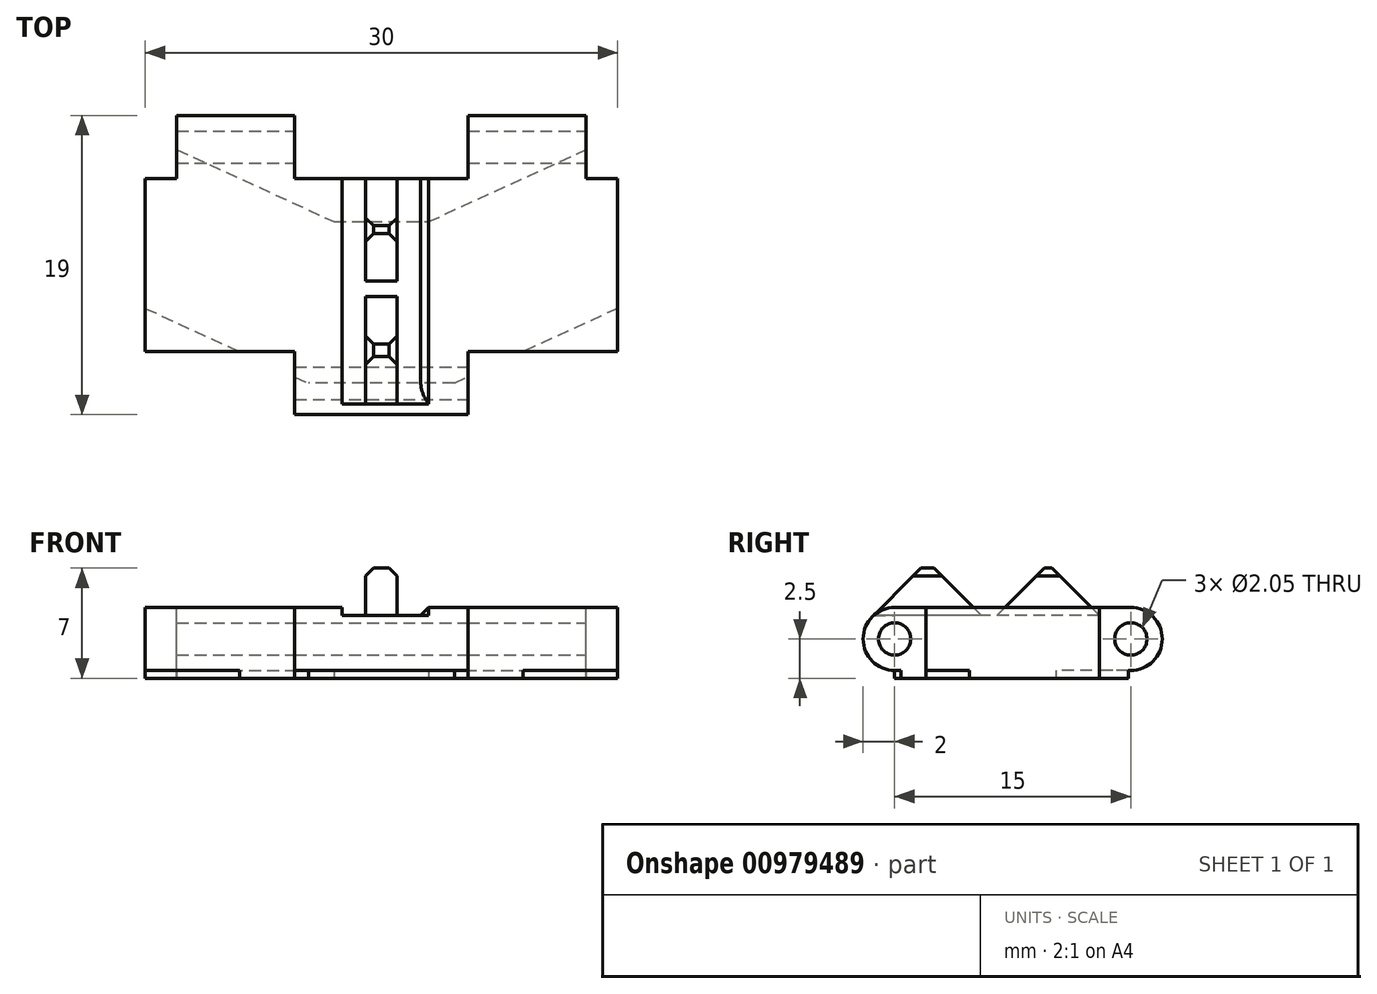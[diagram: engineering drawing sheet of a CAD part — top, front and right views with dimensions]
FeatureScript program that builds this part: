
annotation { "Feature Type Name" : "Feature", "Feature Type Description" : "" }
export const myFeature = defineFeature(function(context is Context, id is Id, definition is map)
    precondition{}
    {
        {
            var Q0;
            Q0=qCreatedBy(makeId("Top.planeOp"),FACE);
            var sketch = newSketch(context, id + "F0", { "sketchPlane" : qUnion([Q0])});
            skLineSegment(sketch, "E0.bottom", {"start": v(15, -7.5) * mm, "end": v(-15, -7.5) * mm});
            skLineSegment(sketch, "E0.top", {"start": v(15, 7.5) * mm, "end": v(-15, 7.5) * mm});
            skLineSegment(sketch, "E0.left", {"start": v(15, -7.5) * mm, "end": v(15, 7.5) * mm});
            skLineSegment(sketch, "E0.right", {"start": v(-15, -7.5) * mm, "end": v(-15, 7.5) * mm});
            skPoint(sketch, "E0.middle", {"position": v(0, 0) * mm});
            skSolve(sketch);
        }
        {
            var Q0;
            Q0=makeQuery(id+"F0.imprint","IMPRINT",FACE,{"disambiguationData":[TD([[makeQuery(id+"F0.imprint","IMPRINT",EDGE,{"derivedFrom":sQuery(id+"F0.wireOp",EDGE,"E0.bottom")}),-1.0]])]});
            extrude(context, id + "F1", {"entities" : qUnion([Q0]), "depth" : 4.5 * mm, "offsetDistance" : 25 * mm});
        }
        {
            var Q0;
            Q0=makeQuery(id+"F1.opExtrude","SWEPT_FACE",FACE,{"disambiguationData":[OSD([sQuery(id+"F0.wireOp",EDGE,"E0.right")])]});
            var sketch = newSketch(context, id + "F2", { "sketchPlane" : qUnion([Q0])});
            skCircle(sketch, "E1", {"center": v(-7.5, 2.5) * mm, "radius": 2 * mm});
            skCircle(sketch, "E2", {"center": v(7.5, 2.5) * mm, "radius": 2 * mm});
            skSolve(sketch);
        }
        {
            var Q0;
            {var subQ0=sQuery(id+"F2.wireOp",EDGE,"vetQoRZT-xKbi-iN1l-QBYZ-xdwohGv9bb5s");var subQ1=sQuery(id+"F0.wireOp",EDGE,"E0.right");var subQ2=makeQuery(id+"F1.opExtrude","SWEPT_EDGE",EDGE,{"disambiguationData":[OSD([sQuery(id+"F0.wireOp",EDGE,"E0.top"),subQ1])]});var subQ3=makeQuery(id+"F2.imprint","INTERSECT",VERTEX,{"disambiguationData":[OD(0.0)],"derivedFrom":[subQ2,subQ0]});Q0=makeQuery(id+"F2.imprint","IMPRINT",FACE,{"disambiguationData":[TD([[makeQuery(id+"F2.imprint","IMPRINT",EDGE,{"disambiguationData":[TD([[subQ3,-1.0]])],"derivedFrom":subQ0}),-1.0]])]});}
            var Q1;
            {var subQ0=sQuery(id+"F2.wireOp",EDGE,"k2q76aXO-4BDj-htHJ-C2at-5MqpkDl38XXc");var subQ1=sQuery(id+"F0.wireOp",EDGE,"E0.right");var subQ2=makeQuery(id+"F1.opExtrude","SWEPT_EDGE",EDGE,{"disambiguationData":[OSD([sQuery(id+"F0.wireOp",EDGE,"E0.bottom"),subQ1])]});var subQ3=makeQuery(id+"F2.imprint","INTERSECT",VERTEX,{"disambiguationData":[OD(0.0)],"derivedFrom":[subQ2,subQ0]});Q1=makeQuery(id+"F2.imprint","IMPRINT",FACE,{"disambiguationData":[TD([[makeQuery(id+"F2.imprint","IMPRINT",EDGE,{"disambiguationData":[TD([[subQ3,1.0]])],"derivedFrom":subQ0}),-1.0]])]});}
            var Q2;
            {var subQ0=sQuery(id+"F2.wireOp",EDGE,"E1");var subQ1=sQuery(id+"F0.wireOp",EDGE,"E0.right");var subQ2=makeQuery(id+"F1.opExtrude","SWEPT_EDGE",EDGE,{"disambiguationData":[OSD([sQuery(id+"F0.wireOp",EDGE,"E0.top"),subQ1])]});var subQ4=makeQuery(id+"F2.imprint","INTERSECT",VERTEX,{"derivedFrom":[subQ2,subQ0]});Q2=makeQuery(id+"F2.imprint","IMPRINT",FACE,{"disambiguationData":[TD([[makeQuery(id+"F2.imprint","IMPRINT",EDGE,{"disambiguationData":[TD([[subQ4,1.0]])],"derivedFrom":subQ0}),1.0]])]});}
            var Q3;
            {var subQ0=sQuery(id+"F2.wireOp",EDGE,"E1");var subQ1=sQuery(id+"F0.wireOp",EDGE,"E0.right");var subQ2=makeQuery(id+"F1.opExtrude","SWEPT_EDGE",EDGE,{"disambiguationData":[OSD([sQuery(id+"F0.wireOp",EDGE,"E0.top"),subQ1])]});var subQ4=makeQuery(id+"F2.imprint","INTERSECT",VERTEX,{"derivedFrom":[subQ2,subQ0]});Q3=makeQuery(id+"F2.imprint","IMPRINT",FACE,{"disambiguationData":[TD([[makeQuery(id+"F2.imprint","IMPRINT",EDGE,{"disambiguationData":[TD([[subQ4,-1.0]])],"derivedFrom":subQ0}),1.0]])]});}
            var Q4;
            {var subQ0=sQuery(id+"F2.wireOp",EDGE,"E2");var subQ1=sQuery(id+"F0.wireOp",EDGE,"E0.right");var subQ2=makeQuery(id+"F1.opExtrude","SWEPT_EDGE",EDGE,{"disambiguationData":[OSD([sQuery(id+"F0.wireOp",EDGE,"E0.bottom"),subQ1])]});var subQ4=makeQuery(id+"F2.imprint","INTERSECT",VERTEX,{"derivedFrom":[subQ2,subQ0]});Q4=makeQuery(id+"F2.imprint","IMPRINT",FACE,{"disambiguationData":[TD([[makeQuery(id+"F2.imprint","IMPRINT",EDGE,{"disambiguationData":[TD([[subQ4,-1.0]])],"derivedFrom":subQ0}),1.0]])]});}
            extrude(context, id + "F3", {"entities" : qUnion([Q0, Q1, Q2, Q3, Q4]), "operationType" : NewBodyOperationType.ADD, "oppositeDirection" : true, "depth" : 30 * mm, "offsetDistance" : 25 * mm});
        }
        {
            var Q0;
            Q0=makeQuery(id+"F1.opExtrude","CAP_FACE",FACE,{"disambiguationData":[OSD([sQuery(id+"F0.wireOp",EDGE,"E0.bottom"),sQuery(id+"F0.wireOp",EDGE,"E0.top"),sQuery(id+"F0.wireOp",EDGE,"E0.left"),sQuery(id+"F0.wireOp",EDGE,"E0.right")])],"isStart":false});
            var sketch = newSketch(context, id + "F4", { "sketchPlane" : qUnion([Q0])});
            skLineSegment(sketch, "E3.bottom", {"start": v(-13, 7.5) * mm, "end": v(-5.5, 7.5) * mm});
            skLineSegment(sketch, "E3.top", {"start": v(-13, 9.5) * mm, "end": v(-5.5, 9.5) * mm});
            skLineSegment(sketch, "E3.left", {"start": v(-13, 7.5) * mm, "end": v(-13, 9.5) * mm});
            skLineSegment(sketch, "E3.right", {"start": v(-5.5, 7.5) * mm, "end": v(-5.5, 9.5) * mm});
            skLineSegment(sketch, "E4.bottom", {"start": v(5.5, 7.5) * mm, "end": v(13, 7.5) * mm});
            skLineSegment(sketch, "E4.top", {"start": v(5.5, 9.5) * mm, "end": v(13, 9.5) * mm});
            skLineSegment(sketch, "E4.left", {"start": v(5.5, 7.5) * mm, "end": v(5.5, 9.5) * mm});
            skLineSegment(sketch, "E4.right", {"start": v(13, 7.5) * mm, "end": v(13, 9.5) * mm});
            skLineSegment(sketch, "E5.bottom", {"start": v(-5.5, -7.5) * mm, "end": v(5.5, -7.5) * mm});
            skLineSegment(sketch, "E5.top", {"start": v(-5.5, -9.5) * mm, "end": v(5.5, -9.5) * mm});
            skLineSegment(sketch, "E5.left", {"start": v(-5.5, -7.5) * mm, "end": v(-5.5, -9.5) * mm});
            skLineSegment(sketch, "E5.right", {"start": v(5.5, -7.5) * mm, "end": v(5.5, -9.5) * mm});
            skLineSegment(sketch, "E6", {"start": v(13, 9.5) * mm, "end": v(15, 9.5) * mm});
            skLineSegment(sketch, "E7", {"start": v(15, 9.5) * mm, "end": v(15, 7.5) * mm});
            skLineSegment(sketch, "E8", {"start": v(15, 7.5) * mm, "end": v(13, 7.5) * mm});
            skLineSegment(sketch, "E9", {"start": v(-13, 9.5) * mm, "end": v(-15, 9.5) * mm});
            skLineSegment(sketch, "E10", {"start": v(-15, 9.5) * mm, "end": v(-15, 7.5) * mm});
            skLineSegment(sketch, "E11", {"start": v(-15, 7.5) * mm, "end": v(-13, 7.5) * mm});
            skLineSegment(sketch, "E12", {"start": v(-5.5, -9.5) * mm, "end": v(-15, -9.5) * mm});
            skLineSegment(sketch, "E13", {"start": v(-15, -9.5) * mm, "end": v(-15, -7.5) * mm});
            skLineSegment(sketch, "E14", {"start": v(-15, -7.5) * mm, "end": v(-5.5, -7.5) * mm});
            skLineSegment(sketch, "E15", {"start": v(5.5, -7.5) * mm, "end": v(15, -7.5) * mm});
            skLineSegment(sketch, "E16", {"start": v(15, -7.5) * mm, "end": v(15, -9.5) * mm});
            skLineSegment(sketch, "E17", {"start": v(15, -9.5) * mm, "end": v(5.5, -9.5) * mm});
            skLineSegment(sketch, "E18", {"start": v(-5.5, 9.5) * mm, "end": v(5.5, 9.5) * mm});
            skSolve(sketch);
        }
        {
            var Q0;
            Q0=makeQuery(id+"F4.imprint","IMPRINT",FACE,{"disambiguationData":[TD([[makeQuery(id+"F4.imprint","IMPRINT",EDGE,{"derivedFrom":sQuery(id+"F4.wireOp",EDGE,"E5.left")}),-1.0]])]});
            var Q1;
            Q1=makeQuery(id+"F4.imprint","IMPRINT",FACE,{"disambiguationData":[TD([[makeQuery(id+"F4.imprint","IMPRINT",EDGE,{"derivedFrom":sQuery(id+"F4.wireOp",EDGE,"E5.right")}),1.0]])]});
            var Q2;
            Q2=makeQuery(id+"F4.imprint","IMPRINT",FACE,{"disambiguationData":[TD([[makeQuery(id+"F4.imprint","IMPRINT",EDGE,{"derivedFrom":sQuery(id+"F4.wireOp",EDGE,"E3.left")}),1.0]])]});
            var Q3;
            Q3=makeQuery(id+"F4.imprint","IMPRINT",FACE,{"disambiguationData":[TD([[makeQuery(id+"F4.imprint","IMPRINT",EDGE,{"derivedFrom":sQuery(id+"F4.wireOp",EDGE,"E4.right")}),-1.0]])]});
            var Q4;
            {var subQ0=sQuery(id+"F4.wireOp",EDGE,"E3.right");Q4=makeQuery(id+"F4.imprint","IMPRINT",FACE,{"disambiguationData":[TD([[makeQuery(id+"F4.imprint","IMPRINT",EDGE,{"derivedFrom":subQ0}),-1.0]])]});}
            extrude(context, id + "F5", {"entities" : qUnion([Q0, Q1, Q2, Q3, Q4]), "operationType" : NewBodyOperationType.REMOVE, "oppositeDirection" : true, "depth" : 25 * mm, "offsetDistance" : 25 * mm});
        }
        {
            var Q0;
            Q0=makeQuery(id+"F3.boolean.opBoolean","MERGE",FACE,{"derivedFrom":[makeQuery(id+"F1.opExtrude","SWEPT_FACE",FACE,{"disambiguationData":[OSD([sQuery(id+"F0.wireOp",EDGE,"E0.left")])]}),makeQuery(id+"F3.opExtrude","CAP_FACE",FACE,{"disambiguationData":[OSD([sQuery(id+"F2.wireOp",EDGE,"E1")])],"isStart":false}),makeQuery(id+"F3.opExtrude","CAP_FACE",FACE,{"disambiguationData":[OSD([sQuery(id+"F0.wireOp",EDGE,"E0.bottom"),sQuery(id+"F0.wireOp",EDGE,"E0.right"),sQuery(id+"F2.wireOp",EDGE,"E2")])],"isStart":false})]});
            var sketch = newSketch(context, id + "F6", { "sketchPlane" : qUnion([Q0])});
            skCircle(sketch, "E19", {"center": v(-7.5, 2.5) * mm, "radius": 1.02 * mm});
            skCircle(sketch, "E20", {"center": v(7.5, 2.5) * mm, "radius": 1.02 * mm});
            skSolve(sketch);
        }
        {
            var Q0;
            Q0 = qSketchRegion(id + "F6", true);
            extrude(context, id + "F7", {"entities" : qUnion([Q0]), "operationType" : NewBodyOperationType.REMOVE, "oppositeDirection" : true, "depth" : 30 * mm, "offsetDistance" : 25 * mm});
        }
        {
            var Q0;
            Q0=makeQuery(id+"F1.opExtrude","CAP_FACE",FACE,{"disambiguationData":[OSD([sQuery(id+"F0.wireOp",EDGE,"E0.bottom"),sQuery(id+"F0.wireOp",EDGE,"E0.top"),sQuery(id+"F0.wireOp",EDGE,"E0.left"),sQuery(id+"F0.wireOp",EDGE,"E0.right")])],"isStart":false});
            var sketch = newSketch(context, id + "F8", { "sketchPlane" : qUnion([Q0])});
            skLineSegment(sketch, "E21.bottom", {"start": v(-5.5, -7.5) * mm, "end": v(-15, -7.5) * mm});
            skLineSegment(sketch, "E21.top", {"start": v(-5.5, -5.5) * mm, "end": v(-15, -5.5) * mm});
            skLineSegment(sketch, "E21.left", {"start": v(-5.5, -7.5) * mm, "end": v(-5.5, -5.5) * mm});
            skLineSegment(sketch, "E21.right", {"start": v(-15, -7.5) * mm, "end": v(-15, -5.5) * mm});
            skLineSegment(sketch, "E22.bottom", {"start": v(5.5, -7.5) * mm, "end": v(15, -7.5) * mm});
            skLineSegment(sketch, "E22.top", {"start": v(5.5, -5.5) * mm, "end": v(15, -5.5) * mm});
            skLineSegment(sketch, "E22.left", {"start": v(5.5, -7.5) * mm, "end": v(5.5, -5.5) * mm});
            skLineSegment(sketch, "E22.right", {"start": v(15, -7.5) * mm, "end": v(15, -5.5) * mm});
            skSolve(sketch);
        }
        {
            var Q0;
            Q0=makeQuery(id+"F8.imprint","IMPRINT",FACE,{"disambiguationData":[TD([[makeQuery(id+"F8.imprint","IMPRINT",EDGE,{"derivedFrom":sQuery(id+"F8.wireOp",EDGE,"E21.bottom")}),-1.0]])]});
            var Q1;
            Q1=makeQuery(id+"F8.imprint","IMPRINT",FACE,{"disambiguationData":[TD([[makeQuery(id+"F8.imprint","IMPRINT",EDGE,{"derivedFrom":sQuery(id+"F8.wireOp",EDGE,"E22.bottom")}),-1.0]])]});
            extrude(context, id + "F9", {"entities" : qUnion([Q0, Q1]), "operationType" : NewBodyOperationType.REMOVE, "oppositeDirection" : true, "depth" : 25 * mm, "offsetDistance" : 25 * mm});
        }
        {
            var Q0;
            Q0=makeQuery(id+"F1.opExtrude","CAP_FACE",FACE,{"disambiguationData":[OSD([sQuery(id+"F0.wireOp",EDGE,"E0.bottom"),sQuery(id+"F0.wireOp",EDGE,"E0.top"),sQuery(id+"F0.wireOp",EDGE,"E0.left"),sQuery(id+"F0.wireOp",EDGE,"E0.right")])],"isStart":false});
            var sketch = newSketch(context, id + "F10", { "sketchPlane" : qUnion([Q0])});
            skLineSegment(sketch, "E23.bottom", {"start": v(-5.5, 7.5) * mm, "end": v(5.5, 7.5) * mm});
            skLineSegment(sketch, "E23.top", {"start": v(-5.5, 5.5) * mm, "end": v(5.5, 5.5) * mm});
            skLineSegment(sketch, "E23.left", {"start": v(-5.5, 7.5) * mm, "end": v(-5.5, 5.5) * mm});
            skLineSegment(sketch, "E23.right", {"start": v(5.5, 7.5) * mm, "end": v(5.5, 5.5) * mm});
            skSolve(sketch);
        }
        {
            var Q0;
            Q0=makeQuery(id+"F10.imprint","IMPRINT",FACE,{"disambiguationData":[TD([[makeQuery(id+"F10.imprint","IMPRINT",EDGE,{"derivedFrom":sQuery(id+"F10.wireOp",EDGE,"E23.bottom")}),1.0]])]});
            extrude(context, id + "F11", {"entities" : qUnion([Q0]), "operationType" : NewBodyOperationType.REMOVE, "oppositeDirection" : true, "depth" : 25 * mm, "offsetDistance" : 25 * mm});
        }
        {
            var Q0;
            Q0=makeQuery(id+"F1.opExtrude","CAP_FACE",FACE,{"disambiguationData":[OSD([sQuery(id+"F0.wireOp",EDGE,"E0.bottom"),sQuery(id+"F0.wireOp",EDGE,"E0.top"),sQuery(id+"F0.wireOp",EDGE,"E0.left"),sQuery(id+"F0.wireOp",EDGE,"E0.right")])],"isStart":false});
            var sketch = newSketch(context, id + "F12", { "sketchPlane" : qUnion([Q0])});
            skLineSegment(sketch, "E24.bottom", {"start": v(-13, 7.5) * mm, "end": v(-15, 7.5) * mm});
            skLineSegment(sketch, "E24.top", {"start": v(-13, 5.5) * mm, "end": v(-15, 5.5) * mm});
            skLineSegment(sketch, "E24.left", {"start": v(-13, 7.5) * mm, "end": v(-13, 5.5) * mm});
            skLineSegment(sketch, "E24.right", {"start": v(-15, 7.5) * mm, "end": v(-15, 5.5) * mm});
            skLineSegment(sketch, "E25.bottom", {"start": v(15, 7.5) * mm, "end": v(13, 7.5) * mm});
            skLineSegment(sketch, "E25.top", {"start": v(15, 5.5) * mm, "end": v(13, 5.5) * mm});
            skLineSegment(sketch, "E25.left", {"start": v(15, 7.5) * mm, "end": v(15, 5.5) * mm});
            skLineSegment(sketch, "E25.right", {"start": v(13, 7.5) * mm, "end": v(13, 5.5) * mm});
            skSolve(sketch);
        }
        {
            var Q0;
            Q0=makeQuery(id+"F12.imprint","IMPRINT",FACE,{"disambiguationData":[TD([[makeQuery(id+"F12.imprint","IMPRINT",EDGE,{"derivedFrom":sQuery(id+"F12.wireOp",EDGE,"E24.bottom")}),1.0]])]});
            var Q1;
            Q1=makeQuery(id+"F12.imprint","IMPRINT",FACE,{"disambiguationData":[TD([[makeQuery(id+"F12.imprint","IMPRINT",EDGE,{"derivedFrom":sQuery(id+"F12.wireOp",EDGE,"E25.bottom")}),1.0]])]});
            extrude(context, id + "F13", {"entities" : qUnion([Q0, Q1]), "operationType" : NewBodyOperationType.REMOVE, "oppositeDirection" : true, "depth" : 25 * mm, "offsetDistance" : 25 * mm});
        }
        {
            var Q0;
            Q0=makeQuery(id+"F1.opExtrude","CAP_FACE",FACE,{"disambiguationData":[OSD([sQuery(id+"F0.wireOp",EDGE,"E0.bottom"),sQuery(id+"F0.wireOp",EDGE,"E0.top"),sQuery(id+"F0.wireOp",EDGE,"E0.left"),sQuery(id+"F0.wireOp",EDGE,"E0.right")])],"isStart":true});
            var sketch = newSketch(context, id + "F14", { "sketchPlane" : qUnion([Q0])});
            skLineSegment(sketch, "E26", {"start": v(0, 5.5) * mm, "end": v(-3, 5.5) * mm});
            skLineSegment(sketch, "E27", {"start": v(-3, 5.5) * mm, "end": v(0, 5.5) * mm});
            skLineSegment(sketch, "E28", {"start": v(0, 5.5) * mm, "end": v(3, 5.5) * mm});
            skLineSegment(sketch, "E29", {"start": v(3, 5.5) * mm, "end": v(15, 0) * mm});
            skLineSegment(sketch, "E30", {"start": v(-15, 0) * mm, "end": v(-3, 5.5) * mm});
            skLineSegment(sketch, "E31", {"start": v(-15, -5.5) * mm, "end": v(-3, 0) * mm});
            skLineSegment(sketch, "E32", {"start": v(-3, 0) * mm, "end": v(3, 0) * mm});
            skLineSegment(sketch, "E33", {"start": v(3, 0) * mm, "end": v(15, -5.5) * mm});
            skLineSegment(sketch, "E34", {"start": v(-15, 2.75) * mm, "end": v(-9, 5.5) * mm});
            skPoint(sketch, "E35.startSnap0", {"position": v(9, 2.75) * mm});
            skLineSegment(sketch, "E36", {"start": v(15, 2.75) * mm, "end": v(9, 5.5) * mm});
            skLineSegment(sketch, "E37", {"start": v(-15, -8.25) * mm, "end": v(-3, -2.75) * mm});
            skLineSegment(sketch, "E38", {"start": v(-3, -2.75) * mm, "end": v(3, -2.75) * mm});
            skLineSegment(sketch, "E39", {"start": v(3, -2.75) * mm, "end": v(15, -8.25) * mm});
            skLineSegment(sketch, "E40", {"start": v(-9, 5.5) * mm, "end": v(-3, 8.25) * mm});
            skLineSegment(sketch, "E41", {"start": v(-3, 8.25) * mm, "end": v(3, 8.25) * mm});
            skLineSegment(sketch, "E42", {"start": v(3, 8.25) * mm, "end": v(9, 5.5) * mm});
            skSolve(sketch);
        }
        {
            var Q0;
            Q0=makeQuery(id+"F14.imprint","IMPRINT",FACE,{"disambiguationData":[TD([[makeQuery(id+"F14.imprint","IMPRINT",EDGE,{"derivedFrom":sQuery(id+"F14.wireOp",EDGE,"E27")}),-1.0]])]});
            var Q1;
            {var subQ0=sQuery(id+"F14.wireOp",EDGE,"E34");Q1=makeQuery(id+"F14.imprint","IMPRINT",FACE,{"disambiguationData":[TD([[makeQuery(id+"F14.imprint","IMPRINT",EDGE,{"derivedFrom":subQ0}),1.0]])]});}
            var Q2;
            {var subQ0=sQuery(id+"F14.wireOp",EDGE,"E36");Q2=makeQuery(id+"F14.imprint","IMPRINT",FACE,{"disambiguationData":[TD([[makeQuery(id+"F14.imprint","IMPRINT",EDGE,{"derivedFrom":subQ0}),-1.0]])]});}
            var Q3;
            {var subQ1=sQuery(id+"F14.wireOp",EDGE,"E38");Q3=makeQuery(id+"F14.imprint","IMPRINT",FACE,{"disambiguationData":[TD([[makeQuery(id+"F14.imprint","IMPRINT",EDGE,{"derivedFrom":subQ1}),-1.0]])]});}
            var Q4;
            {var subQ0=sQuery(id+"F14.wireOp",EDGE,"E40");var subQ3=makeQuery(id+"F5.boolean.opBoolean","INTERSECT",EDGE,{"derivedFrom":[makeQuery(id+"F5.opExtrude","SWEPT_FACE",FACE,{"disambiguationData":[OSD([sQuery(id+"F4.wireOp",EDGE,"E14")])]}),makeQuery(id+"F5.opExtrude","SWEPT_FACE",FACE,{"disambiguationData":[OSD([sQuery(id+"F4.wireOp",EDGE,"E15")])]})]});var subQ4=makeQuery(id+"F14.imprint","INTERSECT",VERTEX,{"derivedFrom":[subQ3,subQ0]});Q4=makeQuery(id+"F14.imprint","IMPRINT",FACE,{"disambiguationData":[TD([[makeQuery(id+"F14.imprint","IMPRINT",EDGE,{"disambiguationData":[TD([[subQ4,1.0]])],"derivedFrom":subQ0}),1.0]])]});}
            var Q5;
            {var subQ0=sQuery(id+"F14.wireOp",EDGE,"E42");var subQ1=makeQuery(id+"F5.boolean.opBoolean","INTERSECT",EDGE,{"derivedFrom":[makeQuery(id+"F5.opExtrude","SWEPT_FACE",FACE,{"disambiguationData":[OSD([sQuery(id+"F4.wireOp",EDGE,"E14")])]}),makeQuery(id+"F5.opExtrude","SWEPT_FACE",FACE,{"disambiguationData":[OSD([sQuery(id+"F4.wireOp",EDGE,"E15")])]})]});var subQ2=makeQuery(id+"F14.imprint","INTERSECT",VERTEX,{"derivedFrom":[subQ1,subQ0]});Q5=makeQuery(id+"F14.imprint","IMPRINT",FACE,{"disambiguationData":[TD([[makeQuery(id+"F14.imprint","IMPRINT",EDGE,{"disambiguationData":[TD([[subQ2,-1.0]])],"derivedFrom":subQ0}),1.0]])]});}
            extrude(context, id + "F15", {"entities" : qUnion([Q0, Q1, Q2, Q3, Q4, Q5]), "operationType" : NewBodyOperationType.REMOVE, "oppositeDirection" : true, "depth" : 0.5 * mm, "offsetDistance" : 25 * mm});
        }
        {
            var Q0;
            Q0=makeQuery(id+"F1.opExtrude","CAP_FACE",FACE,{"disambiguationData":[OSD([sQuery(id+"F0.wireOp",EDGE,"E0.bottom"),sQuery(id+"F0.wireOp",EDGE,"E0.top"),sQuery(id+"F0.wireOp",EDGE,"E0.left"),sQuery(id+"F0.wireOp",EDGE,"E0.right")])],"isStart":false});
            var sketch = newSketch(context, id + "F16", { "sketchPlane" : qUnion([Q0])});
            skLineSegment(sketch, "E43.bottom", {"start": v(-2.5, 5.5) * mm, "end": v(2.5, 5.5) * mm});
            skLineSegment(sketch, "E43.left", {"start": v(-2.5, 5.5) * mm, "end": v(-2.5, -7.5) * mm});
            skLineSegment(sketch, "E43.right", {"start": v(2.5, 5.5) * mm, "end": v(2.5, -7.5) * mm});
            skLineSegment(sketch, "E44", {"start": v(-2.5, -7.5) * mm, "end": v(-2.5, -11.32) * mm});
            skLineSegment(sketch, "E45", {"start": v(-2.5, -11.32) * mm, "end": v(2.5, -11.32) * mm});
            skLineSegment(sketch, "E46", {"start": v(2.5, -11.32) * mm, "end": v(2.5, -7.5) * mm});
            skSolve(sketch);
        }
        {
            var Q0;
            Q0=makeQuery(id+"F16.imprint","IMPRINT",FACE,{"disambiguationData":[TD([[makeQuery(id+"F16.imprint","IMPRINT",EDGE,{"derivedFrom":sQuery(id+"F16.wireOp",EDGE,"E43.bottom")}),-1.0]])]});
            var Q1;
            {var subQ0=sQuery(id+"F16.wireOp",EDGE,"E44");Q1=makeQuery(id+"F16.imprint","IMPRINT",FACE,{"disambiguationData":[TD([[makeQuery(id+"F16.imprint","IMPRINT",EDGE,{"derivedFrom":subQ0}),1.0]])]});}
            extrude(context, id + "F17", {"entities" : qUnion([Q0, Q1]), "operationType" : NewBodyOperationType.REMOVE, "oppositeDirection" : true, "depth" : 0.5 * mm, "offsetDistance" : 25 * mm});
        }
        {
            var Q0;
            Q0=makeQuery(id+"F17.boolean.opBoolean","COPY",FACE,{"derivedFrom":makeQuery(id+"F17.opExtrude","CAP_FACE",FACE,{"disambiguationData":[OSD([sQuery(id+"F16.wireOp",EDGE,"E43.bottom"),sQuery(id+"F16.wireOp",EDGE,"E43.left"),sQuery(id+"F16.wireOp",EDGE,"E43.right"),sQuery(id+"F16.wireOp",EDGE,"E44"),sQuery(id+"F16.wireOp",EDGE,"E45"),sQuery(id+"F16.wireOp",EDGE,"E46")])],"isStart":false})});
            var sketch = newSketch(context, id + "F18", { "sketchPlane" : qUnion([Q0])});
            skLineSegment(sketch, "E47.bottom", {"start": v(-1, 5.5) * mm, "end": v(1, 5.5) * mm});
            skLineSegment(sketch, "E47.top", {"start": v(-1, -8.82) * mm, "end": v(1, -8.82) * mm});
            skLineSegment(sketch, "E47.left", {"start": v(-1, 5.5) * mm, "end": v(-1, -8.82) * mm});
            skLineSegment(sketch, "E47.right", {"start": v(1, 5.5) * mm, "end": v(1, -8.82) * mm});
            skSolve(sketch);
        }
        {
            var Q0;
            Q0=makeQuery(id+"F18.imprint","IMPRINT",FACE,{"disambiguationData":[TD([[makeQuery(id+"F18.imprint","IMPRINT",EDGE,{"derivedFrom":sQuery(id+"F18.wireOp",EDGE,"E47.bottom")}),-1.0]])]});
            extrude(context, id + "F19", {"entities" : qUnion([Q0]), "operationType" : NewBodyOperationType.ADD, "depth" : 3 * mm, "offsetDistance" : 25 * mm});
        }
        {
            var Q0;
            Q0=makeQuery(id+"F19.opExtrude","CAP_EDGE",EDGE,{"disambiguationData":[OSD([sQuery(id+"F18.wireOp",EDGE,"E47.top")])],"isStart":false});
            chamfer(context, id + "F20", {"entities" : qUnion([Q0]), "width" : 3 * mm, "tangentPropagation" : true});
        }
        {
            var Q0;
            Q0=makeQuery(id+"F19.opExtrude","CAP_EDGE",EDGE,{"disambiguationData":[OSD([sQuery(id+"F18.wireOp",EDGE,"E47.bottom")])],"isStart":false});
            chamfer(context, id + "F21", {"entities" : qUnion([Q0]), "width" : 3 * mm, "tangentPropagation" : true});
        }
        {
            var Q0;
            Q0=makeQuery(id+"F19.opExtrude","CAP_EDGE",EDGE,{"disambiguationData":[OSD([sQuery(id+"F18.wireOp",EDGE,"E47.left")])],"isStart":false});
            var Q1;
            Q1=makeQuery(id+"F19.opExtrude","CAP_EDGE",EDGE,{"disambiguationData":[OSD([sQuery(id+"F18.wireOp",EDGE,"E47.right")])],"isStart":false});
            chamfer(context, id + "F22", {"entities" : qUnion([Q0, Q1]), "width" : 0.5 * mm, "tangentPropagation" : true});
        }
        {
            var Q0;
            Q0=makeQuery(id+"F17.boolean.opBoolean","COPY",EDGE,{"derivedFrom":makeQuery(id+"F17.opExtrude","CAP_EDGE",EDGE,{"disambiguationData":[OSD([sQuery(id+"F16.wireOp",EDGE,"E43.right"),sQuery(id+"F16.wireOp",EDGE,"E46")])],"isStart":true})});
            var Q1;
            Q1=makeQuery(id+"F17.boolean.opBoolean","COPY",EDGE,{"derivedFrom":makeQuery(id+"F17.opExtrude","CAP_EDGE",EDGE,{"disambiguationData":[OSD([sQuery(id+"F16.wireOp",EDGE,"E43.left"),sQuery(id+"F16.wireOp",EDGE,"E44")])],"isStart":true})});
            chamfer(context, id + "F23", {"entities" : qUnion([Q0, Q1]), "width" : 0.5 * mm, "tangentPropagation" : true});
        }
        {
            var Q0;
            Q0=makeQuery(id+"F19.opExtrude","SWEPT_FACE",FACE,{"disambiguationData":[OSD([sQuery(id+"F18.wireOp",EDGE,"E47.right")])]});
            var sketch = newSketch(context, id + "F24", { "sketchPlane" : qUnion([Q0])});
            skLineSegment(sketch, "E48", {"start": v(-2, 4) * mm, "end": v(-5, 7) * mm});
            skLineSegment(sketch, "E49", {"start": v(-1, 4) * mm, "end": v(2, 7) * mm});
            skLineSegment(sketch, "E50", {"start": v(-1.5, 4) * mm, "end": v(-11.38, 4) * mm});
            skLineSegment(sketch, "E51", {"start": v(-5, 7) * mm, "end": v(2, 7) * mm});
            skLineSegment(sketch, "E52", {"start": v(-2, 4) * mm, "end": v(-1, 4) * mm});
            skSolve(sketch);
        }
        {
            var Q0;
            {var subQ0=sQuery(id+"F24.wireOp",EDGE,"E51");Q0=makeQuery(id+"F24.imprint","IMPRINT",FACE,{"disambiguationData":[TD([[makeQuery(id+"F24.imprint","IMPRINT",EDGE,{"derivedFrom":subQ0}),-1.0]])]});}
            var Q1;
            {var subQ1=sQuery(id+"F24.wireOp",EDGE,"E48");var subQ2=sQuery(id+"F18.wireOp",EDGE,"E47.right");var subQ4=makeQuery(id+"F22.opChamfer","BLEND_EDGE",EDGE,{"blendedFrom":[makeQuery(id+"F19.opExtrude","CAP_EDGE",EDGE,{"disambiguationData":[OSD([subQ2])],"isStart":false}),makeQuery(id+"F19.opExtrude","SWEPT_FACE",FACE,{"disambiguationData":[OSD([subQ2])]})],"blendedInto":[makeQuery(id+"F19.opExtrude","SWEPT_FACE",FACE,{"disambiguationData":[OSD([subQ2])]})]});var subQ5=makeQuery(id+"F24.imprint","INTERSECT",VERTEX,{"derivedFrom":[subQ4,subQ1]});Q1=makeQuery(id+"F24.imprint","IMPRINT",FACE,{"disambiguationData":[TD([[makeQuery(id+"F24.imprint","IMPRINT",EDGE,{"disambiguationData":[TD([[subQ5,1.0]])],"derivedFrom":subQ1}),-1.0]])]});}
            extrude(context, id + "F25", {"entities" : qUnion([Q0, Q1]), "operationType" : NewBodyOperationType.REMOVE, "oppositeDirection" : true, "depth" : 3 * mm, "offsetDistance" : 25 * mm});
        }
    });
